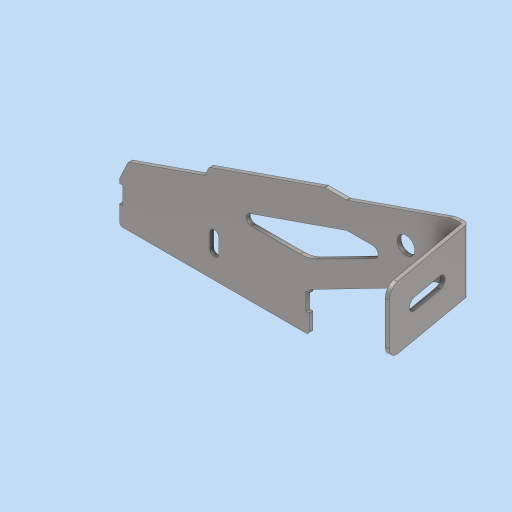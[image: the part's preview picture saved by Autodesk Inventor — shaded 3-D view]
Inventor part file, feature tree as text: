
AUTODESK INVENTOR PART (.ipt)
format: ipt  version: 2023 (Build 270158000, 158)  size: 223,232 bytes
history: native  units: mm
features: other x4, sketch x1, plane x1
ambient origin geometry x8: Origin, YZ Plane, XZ Plane, XY Plane, X Axis, Y Axis, Z Axis, Center Point
bodies: Body1 (feature_tree)
feature tree (6):
  other  "吊架-短(R) - 焊接件-1(v220714).ipt"
  other  "實體1::吊架-短(R) - 焊接件-1(v220714).ipt"
  other  "標籤特徵1"
  sketch  "草圖1"
  plane  "工作平面1"
  other  "實體1"
